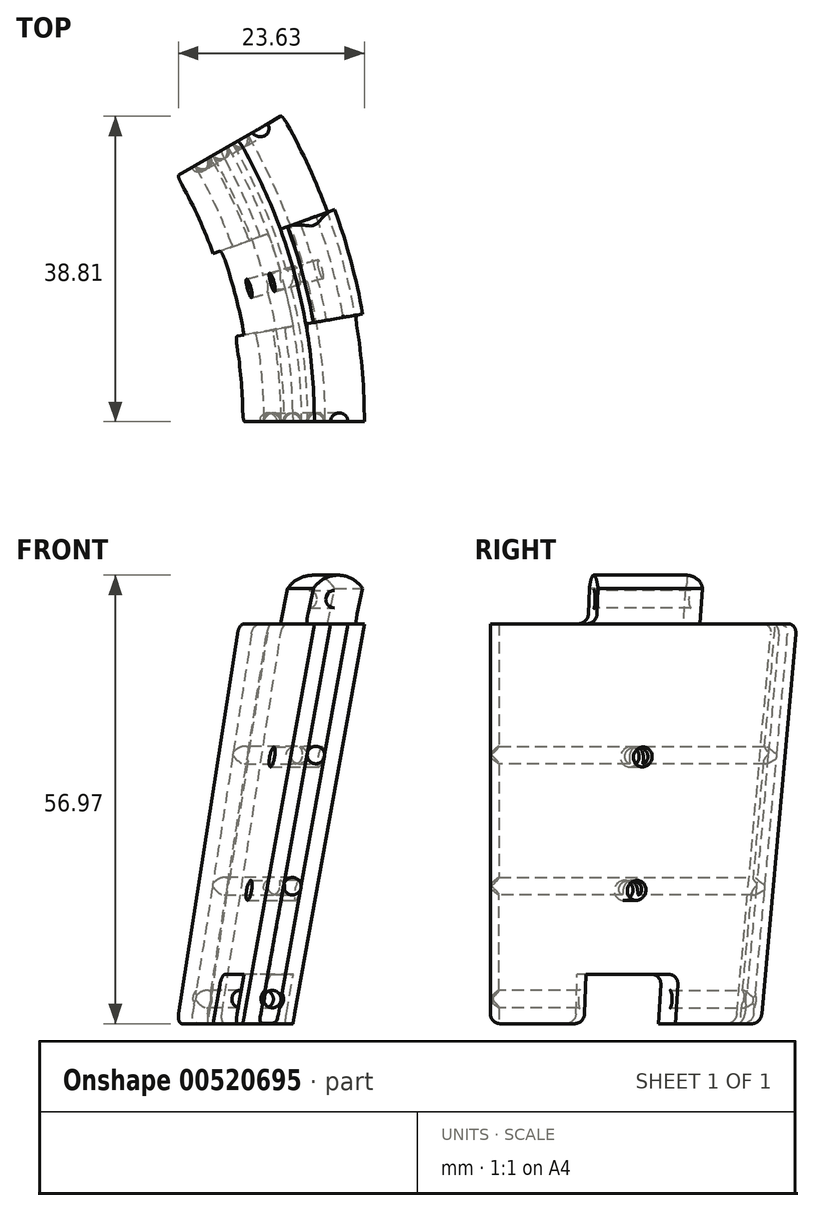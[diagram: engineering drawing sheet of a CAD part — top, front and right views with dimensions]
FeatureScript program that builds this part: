
annotation { "Feature Type Name" : "Feature", "Feature Type Description" : "" }
export const myFeature = defineFeature(function(context is Context, id is Id, definition is map)
    precondition{}
    {
        {
            var Q0;
            Q0=qCreatedBy(makeId("Front.planeOp"),FACE);
            var sketch = newSketch(context, id + "F0", { "sketchPlane" : qUnion([Q0])});
            skLineSegment(sketch, "E0", {"start": v(0, 0) * mm, "end": v(0, 50.8) * mm});
            skLineSegment(sketch, "E1", {"start": v(0, 50.8) * mm, "end": v(77.84, 50.8) * mm});
            skLineSegment(sketch, "E2", {"start": v(0, 0) * mm, "end": v(68.76, 0) * mm});
            skLineSegment(sketch, "E3", {"start": v(68.76, 0) * mm, "end": v(77.84, 50.8) * mm});
            skSolve(sketch);
        }
        {
            var Q0;
            Q0=qSketchRegion(id+"F0",true);
            var Q1;
            Q1=sQuery(id+"F0.wireOp",EDGE,"E0");
            revolve(context, id + "F1", {"entities" : qUnion([Q0]), "axis" : qUnion([Q1]), "revolveType" : RevolveType.ONE_DIRECTION, "angle" : 30 * degree});
        }
        {
            var Q0;
            Q0=makeQuery(id+"F1.opRevolve","CAP_FACE",FACE,{"disambiguationData":[OSD([sQuery(id+"F0.wireOp",EDGE,"E0"),sQuery(id+"F0.wireOp",EDGE,"E1"),sQuery(id+"F0.wireOp",EDGE,"E2"),sQuery(id+"F0.wireOp",EDGE,"E3")])],"isStart":true});
            var sketch = newSketch(context, id + "F2", { "sketchPlane" : qUnion([Q0])});
            skLineSegment(sketch, "E4", {"start": v(0, 0) * mm, "end": v(0, 50.8) * mm});
            skLineSegment(sketch, "E5", {"start": v(0, 50.8) * mm, "end": v(71.49, 50.8) * mm});
            skLineSegment(sketch, "E6", {"start": v(0, 0) * mm, "end": v(62.4, 0) * mm});
            skLineSegment(sketch, "E7", {"start": v(62.4, 0) * mm, "end": v(71.49, 50.8) * mm});
            skSolve(sketch);
        }
        {
            var Q0;
            Q0=qSketchRegion(id+"F2",true);
            var Q1;
            Q1=sQuery(id+"F2.wireOp",EDGE,"E4");
            revolve(context, id + "F3", {"operationType" : NewBodyOperationType.REMOVE, "entities" : qUnion([Q0]), "axis" : qUnion([Q1]), "revolveType" : RevolveType.FULL, "oppositeDirection" : true});
        }
        {
            var Q0;
            Q0=makeQuery(id+"F1.opRevolve","CAP_FACE",FACE,{"disambiguationData":[OSD([sQuery(id+"F0.wireOp",EDGE,"E0"),sQuery(id+"F0.wireOp",EDGE,"E1"),sQuery(id+"F0.wireOp",EDGE,"E2"),sQuery(id+"F0.wireOp",EDGE,"E3")])],"isStart":true});
            var sketch = newSketch(context, id + "F4", { "sketchPlane" : qUnion([Q0])});
            skLineSegment(sketch, "E8", {"start": v(0, 0) * mm, "end": v(0, 50.8) * mm, "construction": true});
            skLineSegment(sketch, "E9", {"start": v(0, 0) * mm, "end": v(68.76, 0) * mm, "construction": true});
            skLineSegment(sketch, "E10", {"start": v(68.76, 0) * mm, "end": v(69.88, 6.25) * mm});
            skLineSegment(sketch, "E11", {"start": v(69.88, 6.25) * mm, "end": v(63.53, 6.25) * mm});
            skLineSegment(sketch, "E12", {"start": v(63.53, 6.25) * mm, "end": v(62.4, 0) * mm});
            skLineSegment(sketch, "E13", {"start": v(68.76, 0) * mm, "end": v(62.4, 0) * mm});
            skSolve(sketch);
        }
        {
            var Q0;
            Q0=qSketchRegion(id+"F4",true);
            var Q1;
            Q1=sQuery(id+"F4.wireOp",EDGE,"E8");
            revolve(context, id + "F5", {"operationType" : NewBodyOperationType.REMOVE, "entities" : qUnion([Q0]), "axis" : qUnion([Q1]), "revolveType" : RevolveType.ONE_DIRECTION, "angle" : 20 * degree});
        }
        {
            var Q0;
            Q0=qSketchRegion(id+"F4",true);
            var Q1;
            Q1=sQuery(id+"F4.wireOp",EDGE,"E8");
            revolve(context, id + "F6", {"operationType" : NewBodyOperationType.ADD, "entities" : qUnion([Q0]), "axis" : qUnion([Q1]), "revolveType" : RevolveType.ONE_DIRECTION, "angle" : 10 * degree});
        }
        {
            var Q0;
            Q0=makeQuery(id+"F6.boolean.opBoolean","MERGE",FACE,{"derivedFrom":[makeQuery(id+"F1.opRevolve","CAP_FACE",FACE,{"disambiguationData":[OSD([sQuery(id+"F0.wireOp",EDGE,"E0"),sQuery(id+"F0.wireOp",EDGE,"E1"),sQuery(id+"F0.wireOp",EDGE,"E2"),sQuery(id+"F0.wireOp",EDGE,"E3")])],"isStart":true}),makeQuery(id+"F6.opRevolve","CAP_FACE",FACE,{"disambiguationData":[OSD([sQuery(id+"F4.wireOp",EDGE,"E10"),sQuery(id+"F4.wireOp",EDGE,"E11"),sQuery(id+"F4.wireOp",EDGE,"E12"),sQuery(id+"F4.wireOp",EDGE,"E13")])],"isStart":true})]});
            var sketch = newSketch(context, id + "F7", { "sketchPlane" : qUnion([Q0])});
            skLineSegment(sketch, "E14", {"start": v(0, 0) * mm, "end": v(0, 50.8) * mm, "construction": true});
            skLineSegment(sketch, "E15", {"start": v(77.84, 50.8) * mm, "end": v(68.76, 0) * mm, "construction": true});
            skLineSegment(sketch, "E16", {"start": v(77.84, 50.8) * mm, "end": v(71.49, 50.8) * mm});
            skLineSegment(sketch, "E17", {"start": v(0, 50.8) * mm, "end": v(0, 101.6) * mm, "construction": true});
            skLineSegment(sketch, "E18", {"start": v(0, 101.6) * mm, "end": v(88.9, 101.6) * mm, "construction": true});
            skLineSegment(sketch, "E19", {"start": v(88.9, 101.6) * mm, "end": v(77.84, 50.8) * mm, "construction": true});
            skLineSegment(sketch, "E20", {"start": v(77.84, 50.8) * mm, "end": v(79.19, 57) * mm});
            skLineSegment(sketch, "E21", {"start": v(79.19, 57) * mm, "end": v(72.84, 57) * mm});
            skLineSegment(sketch, "E22", {"start": v(72.84, 57) * mm, "end": v(71.49, 50.8) * mm});
            skSolve(sketch);
        }
        {
            var Q0;
            Q0=qSketchRegion(id+"F7",true);
            var Q1;
            Q1=sQuery(id+"F7.wireOp",EDGE,"E14");
            revolve(context, id + "F8", {"operationType" : NewBodyOperationType.ADD, "entities" : qUnion([Q0]), "axis" : qUnion([Q1]), "revolveType" : RevolveType.ONE_DIRECTION, "angle" : 20 * degree});
        }
        {
            var Q0;
            Q0=qSketchRegion(id+"F7",true);
            var Q1;
            Q1=sQuery(id+"F7.wireOp",EDGE,"E14");
            revolve(context, id + "F9", {"operationType" : NewBodyOperationType.REMOVE, "entities" : qUnion([Q0]), "axis" : qUnion([Q1]), "revolveType" : RevolveType.ONE_DIRECTION, "angle" : 10 * degree});
        }
        {
            var Q0;
            Q0=makeQuery(id+"F5.boolean.opBoolean","COPY",EDGE,{"derivedFrom":makeQuery(id+"F5.opRevolve","CAP_EDGE",EDGE,{"disambiguationData":[OSD([sQuery(id+"F4.wireOp",EDGE,"E11")])],"isStart":false})});
            var Q1;
            Q1=makeQuery(id+"F6.opRevolve","CAP_EDGE",EDGE,{"disambiguationData":[OSD([sQuery(id+"F4.wireOp",EDGE,"E11")])],"isStart":false});
            var Q2;
            Q2=makeQuery(id+"F6.opRevolve","CAP_EDGE",EDGE,{"disambiguationData":[OSD([sQuery(id+"F4.wireOp",EDGE,"E13")])],"isStart":false});
            var Q3;
            Q3=makeQuery(id+"F5.boolean.opBoolean","COPY",EDGE,{"derivedFrom":makeQuery(id+"F5.opRevolve","CAP_EDGE",EDGE,{"disambiguationData":[OSD([sQuery(id+"F4.wireOp",EDGE,"E13")])],"isStart":false})});
            var Q4;
            Q4=makeQuery(id+"F6.opRevolve","CAP_EDGE",EDGE,{"disambiguationData":[OSD([sQuery(id+"F4.wireOp",EDGE,"E13")])],"isStart":true});
            var Q5;
            Q5=makeQuery(id+"F1.opRevolve","CAP_EDGE",EDGE,{"disambiguationData":[OSD([sQuery(id+"F0.wireOp",EDGE,"E2")])],"isStart":false});
            var Q6;
            Q6=makeQuery(id+"F8.opRevolve","CAP_EDGE",EDGE,{"disambiguationData":[OSD([sQuery(id+"F7.wireOp",EDGE,"E16")])],"isStart":false});
            var Q7;
            Q7=makeQuery(id+"F1.opRevolve","CAP_EDGE",EDGE,{"disambiguationData":[OSD([sQuery(id+"F0.wireOp",EDGE,"E1")])],"isStart":false});
            var Q8;
            Q8=makeQuery(id+"F8.opRevolve","CAP_EDGE",EDGE,{"disambiguationData":[OSD([sQuery(id+"F7.wireOp",EDGE,"E21")])],"isStart":false});
            var Q9;
            Q9=makeQuery(id+"F9.boolean.opBoolean","COPY",EDGE,{"derivedFrom":makeQuery(id+"F9.opRevolve","CAP_EDGE",EDGE,{"disambiguationData":[OSD([sQuery(id+"F7.wireOp",EDGE,"E21")])],"isStart":false})});
            var Q10;
            Q10=makeQuery(id+"F9.boolean.opBoolean","COPY",EDGE,{"derivedFrom":makeQuery(id+"F9.opRevolve","CAP_EDGE",EDGE,{"disambiguationData":[OSD([sQuery(id+"F7.wireOp",EDGE,"E16")])],"isStart":false})});
            var Q11;
            Q11=makeQuery(id+"F9.boolean.opBoolean","COPY",EDGE,{"derivedFrom":makeQuery(id+"F9.opRevolve","CAP_EDGE",EDGE,{"disambiguationData":[OSD([sQuery(id+"F7.wireOp",EDGE,"E16")])],"isStart":true})});
            fillet(context, id + "F10", {"entities" : qUnion([Q0, Q1, Q2, Q3, Q4, Q5, Q6, Q7, Q8, Q9, Q10, Q11]), "radius" : 1.27 * mm, "tangentPropagation" : true, "allowEdgeOverflow" : false});
        }
        {
            var Q0;
            Q0=makeQuery(id+"F8.boolean.opBoolean","MERGE",FACE,{"derivedFrom":[makeQuery(id+"F6.boolean.opBoolean","MERGE",FACE,{"derivedFrom":[makeQuery(id+"F1.opRevolve","CAP_FACE",FACE,{"disambiguationData":[OSD([sQuery(id+"F0.wireOp",EDGE,"E0"),sQuery(id+"F0.wireOp",EDGE,"E1"),sQuery(id+"F0.wireOp",EDGE,"E2"),sQuery(id+"F0.wireOp",EDGE,"E3")])],"isStart":true}),makeQuery(id+"F6.opRevolve","CAP_FACE",FACE,{"disambiguationData":[OSD([sQuery(id+"F4.wireOp",EDGE,"E10"),sQuery(id+"F4.wireOp",EDGE,"E11"),sQuery(id+"F4.wireOp",EDGE,"E12"),sQuery(id+"F4.wireOp",EDGE,"E13")])],"isStart":true})]}),makeQuery(id+"F8.opRevolve","CAP_FACE",FACE,{"disambiguationData":[OSD([sQuery(id+"F7.wireOp",EDGE,"E16"),sQuery(id+"F7.wireOp",EDGE,"E20"),sQuery(id+"F7.wireOp",EDGE,"E21"),sQuery(id+"F7.wireOp",EDGE,"E22")])],"isStart":true})]});
            var sketch = newSketch(context, id + "F11", { "sketchPlane" : qUnion([Q0])});
            skLineSegment(sketch, "E23", {"start": v(0, 0) * mm, "end": v(0, 50.8) * mm, "construction": true});
            skLineSegment(sketch, "E24", {"start": v(0, 50.8) * mm, "end": v(77.84, 50.8) * mm, "construction": true});
            skLineSegment(sketch, "E25", {"start": v(0, 0) * mm, "end": v(68.76, 0) * mm, "construction": true});
            skLineSegment(sketch, "E26", {"start": v(68.76, 0) * mm, "end": v(77.84, 50.8) * mm, "construction": true});
            skLineSegment(sketch, "E27", {"start": v(77.84, 50.8) * mm, "end": v(76.72, 44.55) * mm, "construction": true});
            skLineSegment(sketch, "E28", {"start": v(68.76, 0) * mm, "end": v(69.32, 3.13) * mm, "construction": true});
            skCircle(sketch, "E29", {"center": v(66.14, 3.13) * mm, "radius": 1.11 * mm});
            skLineSegment(sketch, "E30", {"start": v(77.84, 50.8) * mm, "end": v(78.4, 53.93) * mm, "construction": true});
            skLineSegment(sketch, "E31", {"start": v(78.4, 53.93) * mm, "end": v(75.22, 53.93) * mm, "construction": true});
            skCircle(sketch, "E32", {"center": v(75.22, 53.93) * mm, "radius": 1.11 * mm});
            skLineSegment(sketch, "E33", {"start": v(68.76, 0) * mm, "end": v(65.58, 0) * mm, "construction": true});
            skLineSegment(sketch, "E34", {"start": v(65.58, 0) * mm, "end": v(74.66, 50.8) * mm, "construction": true});
            skLineSegment(sketch, "E35", {"start": v(74.66, 50.8) * mm, "end": v(71.68, 34.13) * mm, "construction": true});
            skLineSegment(sketch, "E36", {"start": v(71.68, 34.13) * mm, "end": v(68.7, 17.46) * mm, "construction": true});
            skCircle(sketch, "E37", {"center": v(71.68, 34.13) * mm, "radius": 1.11 * mm});
            skCircle(sketch, "E38", {"center": v(68.7, 17.46) * mm, "radius": 1.11 * mm});
            skSolve(sketch);
        }
        {
            var Q0;
            Q0=qSketchRegion(id+"F11",true);
            var Q1;
            Q1=sQuery(id+"F11.wireOp",EDGE,"E23");
            revolve(context, id + "F12", {"operationType" : NewBodyOperationType.REMOVE, "entities" : qUnion([Q0]), "axis" : qUnion([Q1]), "revolveType" : RevolveType.FULL, "oppositeDirection" : true});
        }
        {
            var Q0;
            Q0=makeQuery(id+"F12.boolean.opBoolean","INTERSECT",EDGE,{"derivedFrom":[makeQuery(id+"F8.boolean.opBoolean","MERGE",FACE,{"derivedFrom":[makeQuery(id+"F6.boolean.opBoolean","MERGE",FACE,{"derivedFrom":[makeQuery(id+"F1.opRevolve","CAP_FACE",FACE,{"disambiguationData":[OSD([sQuery(id+"F0.wireOp",EDGE,"E0"),sQuery(id+"F0.wireOp",EDGE,"E1"),sQuery(id+"F0.wireOp",EDGE,"E2"),sQuery(id+"F0.wireOp",EDGE,"E3")])],"isStart":true}),makeQuery(id+"F6.opRevolve","CAP_FACE",FACE,{"disambiguationData":[OSD([sQuery(id+"F4.wireOp",EDGE,"E10"),sQuery(id+"F4.wireOp",EDGE,"E11"),sQuery(id+"F4.wireOp",EDGE,"E12"),sQuery(id+"F4.wireOp",EDGE,"E13")])],"isStart":true})]}),makeQuery(id+"F8.opRevolve","CAP_FACE",FACE,{"disambiguationData":[OSD([sQuery(id+"F7.wireOp",EDGE,"E16"),sQuery(id+"F7.wireOp",EDGE,"E20"),sQuery(id+"F7.wireOp",EDGE,"E21"),sQuery(id+"F7.wireOp",EDGE,"E22")])],"isStart":true})]}),makeQuery(id+"F12.opRevolve","SWEPT_FACE",FACE,{"disambiguationData":[OSD([sQuery(id+"F11.wireOp",EDGE,"aBI1GnQK-pT2i-Mksw-Z7v4-IHPqoVV2bVJO")])]})]});
            var Q1;
            Q1=makeQuery(id+"F12.boolean.opBoolean","INTERSECT",EDGE,{"derivedFrom":[makeQuery(id+"F8.boolean.opBoolean","MERGE",FACE,{"derivedFrom":[makeQuery(id+"F6.boolean.opBoolean","MERGE",FACE,{"derivedFrom":[makeQuery(id+"F1.opRevolve","CAP_FACE",FACE,{"disambiguationData":[OSD([sQuery(id+"F0.wireOp",EDGE,"E0"),sQuery(id+"F0.wireOp",EDGE,"E1"),sQuery(id+"F0.wireOp",EDGE,"E2"),sQuery(id+"F0.wireOp",EDGE,"E3")])],"isStart":true}),makeQuery(id+"F6.opRevolve","CAP_FACE",FACE,{"disambiguationData":[OSD([sQuery(id+"F4.wireOp",EDGE,"E10"),sQuery(id+"F4.wireOp",EDGE,"E11"),sQuery(id+"F4.wireOp",EDGE,"E12"),sQuery(id+"F4.wireOp",EDGE,"E13")])],"isStart":true})]}),makeQuery(id+"F8.opRevolve","CAP_FACE",FACE,{"disambiguationData":[OSD([sQuery(id+"F7.wireOp",EDGE,"E16"),sQuery(id+"F7.wireOp",EDGE,"E20"),sQuery(id+"F7.wireOp",EDGE,"E21"),sQuery(id+"F7.wireOp",EDGE,"E22")])],"isStart":true})]}),makeQuery(id+"F12.opRevolve","SWEPT_FACE",FACE,{"disambiguationData":[OSD([sQuery(id+"F11.wireOp",EDGE,"E29")])]})]});
            var Q2;
            Q2=makeQuery(id+"F12.boolean.opBoolean","INTERSECT",EDGE,{"derivedFrom":[makeQuery(id+"F1.opRevolve","CAP_FACE",FACE,{"disambiguationData":[OSD([sQuery(id+"F0.wireOp",EDGE,"E0"),sQuery(id+"F0.wireOp",EDGE,"E1"),sQuery(id+"F0.wireOp",EDGE,"E2"),sQuery(id+"F0.wireOp",EDGE,"E3")])],"isStart":false}),makeQuery(id+"F12.opRevolve","SWEPT_FACE",FACE,{"disambiguationData":[OSD([sQuery(id+"F11.wireOp",EDGE,"E29")])]})]});
            var Q3;
            Q3=makeQuery(id+"F12.boolean.opBoolean","INTERSECT",EDGE,{"derivedFrom":[makeQuery(id+"F1.opRevolve","CAP_FACE",FACE,{"disambiguationData":[OSD([sQuery(id+"F0.wireOp",EDGE,"E0"),sQuery(id+"F0.wireOp",EDGE,"E1"),sQuery(id+"F0.wireOp",EDGE,"E2"),sQuery(id+"F0.wireOp",EDGE,"E3")])],"isStart":false}),makeQuery(id+"F12.opRevolve","SWEPT_FACE",FACE,{"disambiguationData":[OSD([sQuery(id+"F11.wireOp",EDGE,"aBI1GnQK-pT2i-Mksw-Z7v4-IHPqoVV2bVJO")])]})]});
            var Q4;
            Q4=makeQuery(id+"F12.boolean.opBoolean","INTERSECT",EDGE,{"derivedFrom":[makeQuery(id+"F9.boolean.opBoolean","COPY",FACE,{"derivedFrom":makeQuery(id+"F9.opRevolve","CAP_FACE",FACE,{"disambiguationData":[OSD([sQuery(id+"F7.wireOp",EDGE,"E16"),sQuery(id+"F7.wireOp",EDGE,"E20"),sQuery(id+"F7.wireOp",EDGE,"E21"),sQuery(id+"F7.wireOp",EDGE,"E22")])],"isStart":false})}),makeQuery(id+"F12.opRevolve","SWEPT_FACE",FACE,{"disambiguationData":[OSD([sQuery(id+"F11.wireOp",EDGE,"E32")])]})]});
            var Q5;
            Q5=makeQuery(id+"F12.boolean.opBoolean","INTERSECT",EDGE,{"derivedFrom":[makeQuery(id+"F8.opRevolve","CAP_FACE",FACE,{"disambiguationData":[OSD([sQuery(id+"F7.wireOp",EDGE,"E16"),sQuery(id+"F7.wireOp",EDGE,"E20"),sQuery(id+"F7.wireOp",EDGE,"E21"),sQuery(id+"F7.wireOp",EDGE,"E22")])],"isStart":false}),makeQuery(id+"F12.opRevolve","SWEPT_FACE",FACE,{"disambiguationData":[OSD([sQuery(id+"F11.wireOp",EDGE,"E32")])]})]});
            var Q6;
            Q6=makeQuery(id+"F12.boolean.opBoolean","INTERSECT",EDGE,{"derivedFrom":[makeQuery(id+"F6.opRevolve","CAP_FACE",FACE,{"disambiguationData":[OSD([sQuery(id+"F4.wireOp",EDGE,"E10"),sQuery(id+"F4.wireOp",EDGE,"E11"),sQuery(id+"F4.wireOp",EDGE,"E12"),sQuery(id+"F4.wireOp",EDGE,"E13")])],"isStart":false}),makeQuery(id+"F12.opRevolve","SWEPT_FACE",FACE,{"disambiguationData":[OSD([sQuery(id+"F11.wireOp",EDGE,"E29")])]})]});
            var Q7;
            Q7=makeQuery(id+"F12.boolean.opBoolean","INTERSECT",EDGE,{"derivedFrom":[makeQuery(id+"F5.boolean.opBoolean","COPY",FACE,{"derivedFrom":makeQuery(id+"F5.opRevolve","CAP_FACE",FACE,{"disambiguationData":[OSD([sQuery(id+"F4.wireOp",EDGE,"E10"),sQuery(id+"F4.wireOp",EDGE,"E11"),sQuery(id+"F4.wireOp",EDGE,"E12"),sQuery(id+"F4.wireOp",EDGE,"E13")])],"isStart":false})}),makeQuery(id+"F12.opRevolve","SWEPT_FACE",FACE,{"disambiguationData":[OSD([sQuery(id+"F11.wireOp",EDGE,"E29")])]})]});
            fillet(context, id + "F13", {"entities" : qUnion([Q0, Q1, Q2, Q3, Q4, Q5, Q6, Q7]), "radius" : 0.32 * mm, "tangentPropagation" : true, "allowEdgeOverflow" : false});
        }
        {
            var Q0;
            Q0=qCreatedBy(makeId("Front.planeOp"),FACE);
            var sketch = newSketch(context, id + "F14", { "sketchPlane" : qUnion([Q0])});
            skLineSegment(sketch, "E39", {"start": v(0, 0) * mm, "end": v(0, 38.2) * mm, "construction": true});
            skSolve(sketch);
        }
        {
            var Q0;
            Q0=makeQuery(id+"F6.opRevolve","SWEPT_FACE",FACE,{"disambiguationData":[OSD([sQuery(id+"F4.wireOp",EDGE,"E13")])]});
            var sketch = newSketch(context, id + "F15", { "sketchPlane" : qUnion([Q0])});
            skLineSegment(sketch, "E40", {"start": v(0, 0) * mm, "end": v(68.75, 0) * mm, "construction": true});
            skPoint(sketch, "E41", {"position": v(65.57, 0) * mm});
            skCircle(sketch, "E42", {"center": v(65.57, 0) * mm, "radius": 1.11 * mm});
            skLineSegment(sketch, "E43", {"start": v(0, 0) * mm, "end": v(59.54, -34.37) * mm, "construction": true});
            skPoint(sketch, "E44", {"position": v(56.79, -32.79) * mm});
            skCircle(sketch, "E45", {"center": v(56.79, -32.79) * mm, "radius": 1.11 * mm});
            skSolve(sketch);
        }
        {
            var Q0;
            Q0=makeQuery(id+"F9.boolean.opBoolean","COPY",FACE,{"derivedFrom":makeQuery(id+"F9.opRevolve","SWEPT_FACE",FACE,{"disambiguationData":[OSD([sQuery(id+"F7.wireOp",EDGE,"E16")])]})});
            var sketch = newSketch(context, id + "F16", { "sketchPlane" : qUnion([Q0])});
            skLineSegment(sketch, "E46", {"start": v(0, 0) * mm, "end": v(77.83, 0) * mm, "construction": true});
            skLineSegment(sketch, "E47", {"start": v(77.83, 0) * mm, "end": v(74.65, 0) * mm, "construction": true});
            skCircle(sketch, "E48", {"center": v(74.65, 0) * mm, "radius": 1.11 * mm});
            skLineSegment(sketch, "E49", {"start": v(0, 0) * mm, "end": v(67.4, 38.91) * mm, "construction": true});
            skPoint(sketch, "E50", {"position": v(64.65, 37.33) * mm});
            skCircle(sketch, "E51", {"center": v(64.65, 37.33) * mm, "radius": 1.11 * mm});
            skSolve(sketch);
        }
        {
            var Q1;
            Q1=makeQuery(id+"F16.imprint","IMPRINT",FACE,{"disambiguationData":[TD([[makeQuery(id+"F16.imprint","IMPRINT",EDGE,{"derivedFrom":sQuery(id+"F16.wireOp",EDGE,"E48")}),1.0]])]});
            var Q2;
            Q2=makeQuery(id+"F15.imprint","IMPRINT",FACE,{"disambiguationData":[TD([[makeQuery(id+"F15.imprint","IMPRINT",EDGE,{"derivedFrom":sQuery(id+"F15.wireOp",EDGE,"E42")}),1.0]])]});
            loft(context, id + "F17", {"operationType" : NewBodyOperationType.REMOVE, "sheetProfilesArray" : [{ "sheetProfileEntities" : qUnion([Q1]) }, { "sheetProfileEntities" : qUnion([Q2]) }]});
        }
        {
            var Q1;
            Q1=makeQuery(id+"F16.imprint","IMPRINT",FACE,{"disambiguationData":[TD([[makeQuery(id+"F16.imprint","IMPRINT",EDGE,{"derivedFrom":sQuery(id+"F16.wireOp",EDGE,"E51")}),1.0]])]});
            var Q2;
            Q2=makeQuery(id+"F15.imprint","IMPRINT",FACE,{"disambiguationData":[TD([[makeQuery(id+"F15.imprint","IMPRINT",EDGE,{"derivedFrom":sQuery(id+"F15.wireOp",EDGE,"E45")}),1.0]])]});
            loft(context, id + "F18", {"operationType" : NewBodyOperationType.REMOVE, "sheetProfilesArray" : [{ "sheetProfileEntities" : qUnion([Q1]) }, { "sheetProfileEntities" : qUnion([Q2]) }]});
        }
        {
            var Q0;
            Q0=qCreatedBy(makeId("Front.planeOp"),FACE);
            var sketch = newSketch(context, id + "F19", { "sketchPlane" : qUnion([Q0])});
            skLineSegment(sketch, "E52", {"start": v(0, 0) * mm, "end": v(68.76, 0) * mm, "construction": true});
            skLineSegment(sketch, "E53", {"start": v(0, 0) * mm, "end": v(0, 50.8) * mm, "construction": true});
            skLineSegment(sketch, "E54", {"start": v(0, 50.8) * mm, "end": v(74.5, 50.8) * mm, "construction": true});
            skLineSegment(sketch, "E55", {"start": v(77.85, 50.8) * mm, "end": v(68.76, 0) * mm, "construction": true});
            skLineSegment(sketch, "E56", {"start": v(0, 50.8) * mm, "end": v(0, 101.6) * mm, "construction": true});
            skLineSegment(sketch, "E57", {"start": v(0, 101.6) * mm, "end": v(88.9, 101.6) * mm, "construction": true});
            skLineSegment(sketch, "E58", {"start": v(88.9, 101.6) * mm, "end": v(77.85, 50.8) * mm, "construction": true});
            skLineSegment(sketch, "E59", {"start": v(77.85, 50.8) * mm, "end": v(71.5, 50.8) * mm, "construction": true});
            skLineSegment(sketch, "E60", {"start": v(77.85, 50.8) * mm, "end": v(78.82, 55.27) * mm, "construction": true});
            skLineSegment(sketch, "E61", {"start": v(72.47, 55.27) * mm, "end": v(71.5, 50.8) * mm, "construction": true});
            skLineSegment(sketch, "E62", {"start": v(78.82, 55.27) * mm, "end": v(79.57, 58.72) * mm});
            skLineSegment(sketch, "E63", {"start": v(79.57, 58.72) * mm, "end": v(72.84, 58.72) * mm});
            skArc(sketch, "E64", {"start": v(78.82, 55.27) * mm, "mid": v(75.65, 56.97) * mm, "end": v(72.47, 55.27) * mm});
            skLineSegment(sketch, "E65", {"start": v(72.47, 55.27) * mm, "end": v(72.13, 55.27) * mm});
            skLineSegment(sketch, "E66", {"start": v(72.13, 55.27) * mm, "end": v(72.84, 58.72) * mm});
            skSolve(sketch);
        }
        {
            var Q0;
            Q0=qSketchRegion(id+"F19",true);
            var Q1;
            Q1=sQuery(id+"F19.wireOp",EDGE,"E53");
            revolve(context, id + "F20", {"operationType" : NewBodyOperationType.REMOVE, "entities" : qUnion([Q0]), "axis" : qUnion([Q1]), "revolveType" : RevolveType.FULL, "oppositeDirection" : true});
        }
        {
            var Q0;
            Q0=qCreatedBy(makeId("Top.planeOp"),FACE);
            cPlane(context, id + "F21", {"entities" : qUnion([Q0]), "cplaneType" : CPlaneType.OFFSET, "offset" : 2 / 76.2 * mm, "width" : 152.4 * mm, "height" : 152.4 * mm});
        }
        {
            var Q0;
            Q0=qCreatedBy(makeId("Right.planeOp"),FACE);
            var sketch = newSketch(context, id + "F22", { "sketchPlane" : qUnion([Q0])});
            skLineSegment(sketch, "E67", {"start": v(0, 0) * mm, "end": v(0, 16.93) * mm, "construction": true});
            skLineSegment(sketch, "E68", {"start": v(0, 16.93) * mm, "end": v(0, 33.88) * mm, "construction": true});
            skCircle(sketch, "E69", {"center": v(0, 33.88) * mm, "radius": 1.27 * mm});
            skCircle(sketch, "E70", {"center": v(0, 16.93) * mm, "radius": 1.27 * mm});
            skSolve(sketch);
        }
        {
            var Q0;
            Q0=qCreatedBy(id+"F21.planeOp",FACE);
            var sketch = newSketch(context, id + "F23", { "sketchPlane" : qUnion([Q0])});
            skLineSegment(sketch, "E71", {"start": v(0, 0) * mm, "end": v(25.4, 0) * mm, "construction": true});
            skLineSegment(sketch, "E72", {"start": v(0, 0) * mm, "end": v(98.14, 26.3) * mm});
            skSolve(sketch);
        }
        {
            var Q0;
            Q0 = qSketchRegion(id + "F22", true);
            var Q1;
            Q1=sQuery(id+"F23.wireOp",EDGE,"E72");
            sweep(context, id + "F24", {"operationType" : NewBodyOperationType.REMOVE, "profiles" : qUnion([Q0]), "path" : qUnion([Q1])});
        }
    });
